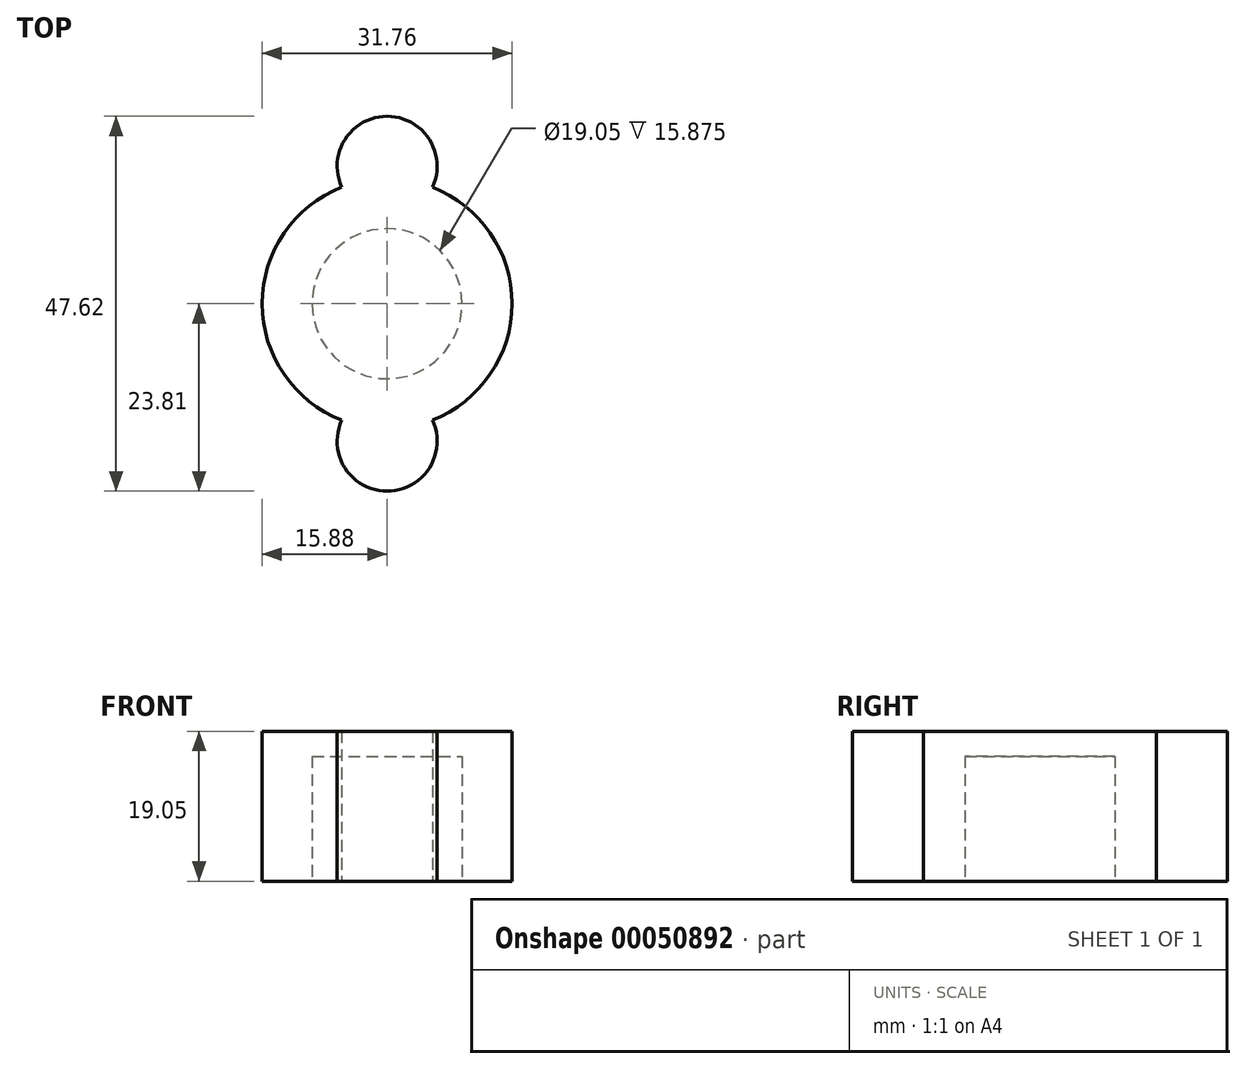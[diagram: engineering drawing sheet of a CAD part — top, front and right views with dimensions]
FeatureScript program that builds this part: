
annotation { "Feature Type Name" : "Feature", "Feature Type Description" : "" }
export const myFeature = defineFeature(function(context is Context, id is Id, definition is map)
    precondition{}
    {
        {
            var Q0;
            Q0=qCreatedBy(makeId("Top.planeOp"),FACE);
            var sketch = newSketch(context, id + "F0", { "sketchPlane" : qUnion([Q0])});
            skArc(sketch, "E0", {"start": v(5.76, -14.8) * mm, "mid": v(15.88, 0) * mm, "end": v(5.76, 14.8) * mm});
            skArc(sketch, "E1", {"start": v(5.76, 14.8) * mm, "mid": v(0, 23.81) * mm, "end": v(-5.76, 14.8) * mm});
            skArc(sketch, "E2", {"start": v(-5.76, -14.8) * mm, "mid": v(0, -23.81) * mm, "end": v(5.76, -14.8) * mm});
            skCircle(sketch, "E3", {"center": v(0, 0) * mm, "radius": 12.7 * mm, "construction": true});
            skLineSegment(sketch, "E4", {"start": v(0, 0) * mm, "end": v(0, 17.46) * mm, "construction": true});
            skLineSegment(sketch, "E5", {"start": v(0, 0) * mm, "end": v(0, -17.46) * mm, "construction": true});
            skArc(sketch, "E6.trimOffspring", {"start": v(-5.76, 14.8) * mm, "mid": v(-15.88, 0) * mm, "end": v(-5.76, -14.8) * mm});
            skSolve(sketch);
        }
        {
            var Q0;
            Q0 = qSketchRegion(id + "F0", true);
            extrude(context, id + "F1", {"entities" : qUnion([Q0]), "depth" : 19.05 * mm});
        }
        {
            var Q0;
            Q0=makeQuery(id+"F1.opExtrude","CAP_FACE",FACE,{"disambiguationData":[OSD([sQuery(id+"F0.wireOp",EDGE,"E0"),sQuery(id+"F0.wireOp",EDGE,"E1"),sQuery(id+"F0.wireOp",EDGE,"E2"),sQuery(id+"F0.wireOp",EDGE,"E6.trimOffspring")])],"isStart":true});
            var sketch = newSketch(context, id + "F2", { "sketchPlane" : qUnion([Q0])});
            skCircle(sketch, "E7", {"center": v(0, 0) * mm, "radius": 9.53 * mm});
            skSolve(sketch);
        }
        {
            var Q0;
            Q0 = qSketchRegion(id + "F2", true);
            extrude(context, id + "F3", {"entities" : qUnion([Q0]), "operationType" : NewBodyOperationType.REMOVE, "oppositeDirection" : true, "depth" : 15.88 * mm});
        }
    });
